FCSTD DOCUMENT  (FreeCAD 1.1R40971 (Git))
Label: pole-barn-interior2
License: All rights reserved
LicenseURL: https://en.wikipedia.org/wiki/All_rights_reserved
objects: App::Point×1, Sketcher::SketchObject×1, PartDesign::Body×1
note: 3 computed .brp shape members not serialized (recipe doc carries the construction recipe); baked Part::Feature solids carry a one-line shape summary decoded from their .brp

FEATURE [App::Point] Origin001
  Role = Origin
FEATURE [Sketcher::SketchObject] Sketch
  ArcFitTolerance = 1e-06
  AttachmentSupport = -> [XY_Plane]
  ExternalTypes = [0]
  FullyConstrained = false
  MakeInternals = false
  MapMode = 5
  sketch-geometry (89):
    g0: LineSegment StartX=4876.8 StartY=439.251 StartZ=0 EndX=4991.1 EndY=439.251 EndZ=0
    g1: LineSegment StartX=4991.1 StartY=439.251 StartZ=0 EndX=4991.1 EndY=629.751 EndZ=0
    g2: LineSegment StartX=4991.1 StartY=629.751 StartZ=0 EndX=4876.8 EndY=629.751 EndZ=0
    g3: LineSegment StartX=4876.8 StartY=629.751 StartZ=0 EndX=4876.8 EndY=439.251 EndZ=0
    g4: LineSegment StartX=-4876.8 StartY=-8343.9 StartZ=0 EndX=4876.8 EndY=-8343.9 EndZ=0
    g5: LineSegment StartX=4876.8 StartY=-8343.9 StartZ=0 EndX=4876.8 EndY=8343.9 EndZ=0
    g6: LineSegment StartX=4876.8 StartY=8343.9 StartZ=0 EndX=-4876.8 EndY=8343.9 EndZ=0
    g7: LineSegment StartX=-4876.8 StartY=8343.9 StartZ=0 EndX=-4876.8 EndY=-8343.9 EndZ=0
    g8: GeomPoint [constr] X=0 Y=0 Z=0
    g9: LineSegment StartX=-5817.55 StartY=9316.89 StartZ=0 EndX=-5703.25 EndY=9316.89 EndZ=0
    g10: LineSegment StartX=-5703.25 StartY=9316.89 StartZ=0 EndX=-5703.25 EndY=9507.39 EndZ=0
    g11: LineSegment StartX=-5703.25 StartY=9507.39 StartZ=0 EndX=-5817.55 EndY=9507.39 EndZ=0
    g12: LineSegment StartX=-5817.55 StartY=9507.39 StartZ=0 EndX=-5817.55 EndY=9316.89 EndZ=0
    g13: LineSegment StartX=-6563.87 StartY=-9198.88 StartZ=0 EndX=-6449.57 EndY=-9198.88 EndZ=0
    g14: LineSegment StartX=-6449.57 StartY=-9198.88 StartZ=0 EndX=-6449.57 EndY=-9008.38 EndZ=0
    g15: LineSegment StartX=-6449.57 StartY=-9008.38 StartZ=0 EndX=-6563.87 EndY=-9008.38 EndZ=0
    g16: LineSegment StartX=-6563.87 StartY=-9008.38 StartZ=0 EndX=-6563.87 EndY=-9198.88 EndZ=0
    g17: LineSegment StartX=6443.37 StartY=-8807.95 StartZ=0 EndX=6557.67 EndY=-8807.95 EndZ=0
    g18: LineSegment StartX=6557.67 StartY=-8807.95 StartZ=0 EndX=6557.67 EndY=-8617.45 EndZ=0
    g19: LineSegment StartX=6557.67 StartY=-8617.45 StartZ=0 EndX=6443.37 EndY=-8617.45 EndZ=0
    g20: LineSegment StartX=6443.37 StartY=-8617.45 StartZ=0 EndX=6443.37 EndY=-8807.95 EndZ=0
    g21: LineSegment StartX=3028.84 StartY=8343.9 StartZ=0 EndX=3143.14 EndY=8343.9 EndZ=0
    g22: LineSegment StartX=3143.14 StartY=8343.9 StartZ=0 EndX=3143.14 EndY=8534.4 EndZ=0
    g23: LineSegment StartX=3143.14 StartY=8534.4 StartZ=0 EndX=3028.84 EndY=8534.4 EndZ=0
    g24: LineSegment StartX=3028.84 StartY=8534.4 StartZ=0 EndX=3028.84 EndY=8343.9 EndZ=0
    g25: LineSegment StartX=1020.89 StartY=8343.9 StartZ=0 EndX=1135.19 EndY=8343.9 EndZ=0
    g26: LineSegment StartX=1135.19 StartY=8343.9 StartZ=0 EndX=1135.19 EndY=8534.4 EndZ=0
    g27: LineSegment StartX=1135.19 StartY=8534.4 StartZ=0 EndX=1020.89 EndY=8534.4 EndZ=0
    g28: LineSegment StartX=1020.89 StartY=8534.4 StartZ=0 EndX=1020.89 EndY=8343.9 EndZ=0
    g29: LineSegment StartX=-1289.14 StartY=8343.9 StartZ=0 EndX=-1174.84 EndY=8343.9 EndZ=0
    g30: LineSegment StartX=-1174.84 StartY=8343.9 StartZ=0 EndX=-1174.84 EndY=8534.4 EndZ=0
    g31: LineSegment StartX=-1174.84 StartY=8534.4 StartZ=0 EndX=-1289.14 EndY=8534.4 EndZ=0
    g32: LineSegment StartX=-1289.14 StartY=8534.4 StartZ=0 EndX=-1289.14 EndY=8343.9 EndZ=0
    g33: LineSegment StartX=-3969.53 StartY=8343.9 StartZ=0 EndX=-3855.23 EndY=8343.9 EndZ=0
    g34: LineSegment StartX=-3855.23 StartY=8343.9 StartZ=0 EndX=-3855.23 EndY=8534.4 EndZ=0
    g35: LineSegment StartX=-3855.23 StartY=8534.4 StartZ=0 EndX=-3969.53 EndY=8534.4 EndZ=0
    g36: LineSegment StartX=-3969.53 StartY=8534.4 StartZ=0 EndX=-3969.53 EndY=8343.9 EndZ=0
    g37: LineSegment StartX=4876.8 StartY=-2521.71 StartZ=0 EndX=4991.1 EndY=-2521.71 EndZ=0
    g38: LineSegment StartX=4991.1 StartY=-2521.71 StartZ=0 EndX=4991.1 EndY=-2331.21 EndZ=0
    g39: LineSegment StartX=4991.1 StartY=-2331.21 StartZ=0 EndX=4876.8 EndY=-2331.21 EndZ=0
    g40: LineSegment StartX=4876.8 StartY=-2331.21 StartZ=0 EndX=4876.8 EndY=-2521.71 EndZ=0
    g41: LineSegment StartX=4876.8 StartY=-6117.69 StartZ=0 EndX=4991.1 EndY=-6117.69 EndZ=0
    g42: LineSegment StartX=4991.1 StartY=-6117.69 StartZ=0 EndX=4991.1 EndY=-5927.19 EndZ=0
    g43: LineSegment StartX=4991.1 StartY=-5927.19 StartZ=0 EndX=4876.8 EndY=-5927.19 EndZ=0
    g44: LineSegment StartX=4876.8 StartY=-5927.19 StartZ=0 EndX=4876.8 EndY=-6117.69 EndZ=0
    g45: LineSegment StartX=3028.84 StartY=-8534.4 StartZ=0 EndX=3143.14 EndY=-8534.4 EndZ=0
    g46: LineSegment StartX=3143.14 StartY=-8534.4 StartZ=0 EndX=3143.14 EndY=-8343.9 EndZ=0
    g47: LineSegment StartX=3143.14 StartY=-8343.9 StartZ=0 EndX=3028.84 EndY=-8343.9 EndZ=0
    g48: LineSegment StartX=3028.84 StartY=-8343.9 StartZ=0 EndX=3028.84 EndY=-8534.4 EndZ=0
    g49: LineSegment StartX=1020.89 StartY=-8534.4 StartZ=0 EndX=1135.19 EndY=-8534.4 EndZ=0
    g50: LineSegment StartX=1135.19 StartY=-8534.4 StartZ=0 EndX=1135.19 EndY=-8343.9 EndZ=0
    g51: LineSegment StartX=1135.19 StartY=-8343.9 StartZ=0 EndX=1020.89 EndY=-8343.9 EndZ=0
    g52: LineSegment StartX=1020.89 StartY=-8343.9 StartZ=0 EndX=1020.89 EndY=-8534.4 EndZ=0
    g53: LineSegment StartX=-2728.47 StartY=-8534.4 StartZ=0 EndX=-2614.17 EndY=-8534.4 EndZ=0
    g54: LineSegment StartX=-2614.17 StartY=-8534.4 StartZ=0 EndX=-2614.17 EndY=-8343.9 EndZ=0
    g55: LineSegment StartX=-2614.17 StartY=-8343.9 StartZ=0 EndX=-2728.47 EndY=-8343.9 EndZ=0
    g56: LineSegment StartX=-2728.47 StartY=-8343.9 StartZ=0 EndX=-2728.47 EndY=-8534.4 EndZ=0
    g57: LineSegment StartX=-4991.1 StartY=-6117.69 StartZ=0 EndX=-4876.8 EndY=-6117.69 EndZ=0
    g58: LineSegment StartX=-4876.8 StartY=-6117.69 StartZ=0 EndX=-4876.8 EndY=-5927.19 EndZ=0
    g59: LineSegment StartX=-4876.8 StartY=-5927.19 StartZ=0 EndX=-4991.1 EndY=-5927.19 EndZ=0
    g60: LineSegment StartX=-4991.1 StartY=-5927.19 StartZ=0 EndX=-4991.1 EndY=-6117.69 EndZ=0
    g61: LineSegment StartX=-4991.1 StartY=-2521.71 StartZ=0 EndX=-4876.8 EndY=-2521.71 EndZ=0
    g62: LineSegment StartX=-4876.8 StartY=-2521.71 StartZ=0 EndX=-4876.8 EndY=-2331.21 EndZ=0
    g63: LineSegment StartX=-4876.8 StartY=-2331.21 StartZ=0 EndX=-4991.1 EndY=-2331.21 EndZ=0
    g64: LineSegment StartX=-4991.1 StartY=-2331.21 StartZ=0 EndX=-4991.1 EndY=-2521.71 EndZ=0
    g65: LineSegment StartX=-4991.1 StartY=3541.08 StartZ=0 EndX=-4876.8 EndY=3541.08 EndZ=0
    g66: LineSegment StartX=-4876.8 StartY=3541.08 StartZ=0 EndX=-4876.8 EndY=3731.58 EndZ=0
    g67: LineSegment StartX=-4876.8 StartY=3731.58 StartZ=0 EndX=-4991.1 EndY=3731.58 EndZ=0
    g68: LineSegment StartX=-4991.1 StartY=3731.58 StartZ=0 EndX=-4991.1 EndY=3541.08 EndZ=0
    g69: LineSegment StartX=-4991.1 StartY=5815.59 StartZ=0 EndX=-4876.8 EndY=5815.59 EndZ=0
    g70: LineSegment StartX=-4876.8 StartY=5815.59 StartZ=0 EndX=-4876.8 EndY=6006.09 EndZ=0
    g71: LineSegment StartX=-4876.8 StartY=6006.09 StartZ=0 EndX=-4991.1 EndY=6006.09 EndZ=0
    g72: LineSegment StartX=-4991.1 StartY=6006.09 StartZ=0 EndX=-4991.1 EndY=5815.59 EndZ=0
    g73: LineSegment StartX=4876.8 StartY=3541.08 StartZ=0 EndX=4991.1 EndY=3541.08 EndZ=0
    g74: LineSegment StartX=4991.1 StartY=3541.08 StartZ=0 EndX=4991.1 EndY=3731.58 EndZ=0
    g75: LineSegment StartX=4991.1 StartY=3731.58 StartZ=0 EndX=4876.8 EndY=3731.58 EndZ=0
    g76: LineSegment StartX=4876.8 StartY=3731.58 StartZ=0 EndX=4876.8 EndY=3541.08 EndZ=0
    g77: LineSegment StartX=4876.8 StartY=5815.59 StartZ=0 EndX=4991.1 EndY=5815.59 EndZ=0
    g78: LineSegment StartX=4991.1 StartY=5815.59 StartZ=0 EndX=4991.1 EndY=6006.09 EndZ=0
    g79: LineSegment StartX=4991.1 StartY=6006.09 StartZ=0 EndX=4876.8 EndY=6006.09 EndZ=0
    g80: LineSegment StartX=4876.8 StartY=6006.09 StartZ=0 EndX=4876.8 EndY=5815.59 EndZ=0
    g81: LineSegment StartX=-4991.1 StartY=439.251 StartZ=0 EndX=-4876.8 EndY=439.251 EndZ=0
    g82: LineSegment StartX=-4876.8 StartY=439.251 StartZ=0 EndX=-4876.8 EndY=629.751 EndZ=0
    g83: LineSegment StartX=-4876.8 StartY=629.751 StartZ=0 EndX=-4991.1 EndY=629.751 EndZ=0
    g84: LineSegment StartX=-4991.1 StartY=629.751 StartZ=0 EndX=-4991.1 EndY=439.251 EndZ=0
    g85: LineSegment StartX=5981.37 StartY=9050.35 StartZ=0 EndX=6095.67 EndY=9050.35 EndZ=0
    g86: LineSegment StartX=6095.67 StartY=9050.35 StartZ=0 EndX=6095.67 EndY=9240.85 EndZ=0
    g87: LineSegment StartX=6095.67 StartY=9240.85 StartZ=0 EndX=5981.37 EndY=9240.85 EndZ=0
    g88: LineSegment StartX=5981.37 StartY=9240.85 StartZ=0 EndX=5981.37 EndY=9050.35 EndZ=0
  constraints (246):
    c: Coincident(g0,g1)
    c: Coincident(g1,g2)
    c: Coincident(g2,g3)
    c: Coincident(g3,g0)
    c: Horizontal(g0)
    c: Horizontal(g2)
    c: Vertical(g1)
    c: Vertical(g3)
    c: Distance(g1,g3) = 114.3
    c: Distance(g0,g2) = 190.5
    c: Coincident(g4,g5)
    c: Coincident(g5,g6)
    c: Coincident(g6,g7)
    c: Coincident(g7,g4)
    c: Horizontal(g4)
    c: Horizontal(g6)
    c: Vertical(g5)
    c: Vertical(g7)
    c: Symmetric(g6,g4,g8)
    c: Distance(g5,g7) = 9753.6
    c: Distance(g4,g6) = 16687.8
    c: Coincident(g8,g-1)
    c: Coincident(g9,g10)
    c: Coincident(g10,g11)
    c: Coincident(g11,g12)
    c: Coincident(g12,g9)
    c: Horizontal(g9)
    c: Horizontal(g11)
    c: Vertical(g10)
    c: Vertical(g12)
    c: Distance(g10,g12) = 114.3
    c: Distance(g9,g11) = 190.5
    c: Coincident(g13,g14)
    c: Coincident(g14,g15)
    c: Coincident(g15,g16)
    c: Coincident(g16,g13)
    c: Horizontal(g13)
    c: Horizontal(g15)
    c: Vertical(g14)
    c: Vertical(g16)
    c: Distance(g14,g16) = 114.3
    c: Distance(g13,g15) = 190.5
    c: Coincident(g17,g18)
    c: Coincident(g18,g19)
    c: Coincident(g19,g20)
    c: Coincident(g20,g17)
    c: Horizontal(g17)
    c: Horizontal(g19)
    c: Vertical(g18)
    c: Vertical(g20)
    c: Distance(g18,g20) = 114.3
    c: Distance(g17,g19) = 190.5
    c: Coincident(g21,g22)
    c: Coincident(g22,g23)
    c: Coincident(g23,g24)
    c: Coincident(g24,g21)
    c: Horizontal(g21)
    c: Horizontal(g23)
    c: Vertical(g22)
    c: Vertical(g24)
    c: Distance(g22,g24) = 114.3
    c: Distance(g21,g23) = 190.5
    c: Coincident(g25,g26)
    c: Coincident(g26,g27)
    c: Coincident(g27,g28)
    c: Coincident(g28,g25)
    c: Horizontal(g25)
    c: Horizontal(g27)
    c: Vertical(g26)
    c: Vertical(g28)
    c: Distance(g26,g28) = 114.3
    c: Distance(g25,g27) = 190.5
    c: Coincident(g29,g30)
    c: Coincident(g30,g31)
    c: Coincident(g31,g32)
    c: Coincident(g32,g29)
    c: Horizontal(g29)
    c: Horizontal(g31)
    c: Vertical(g30)
    c: Vertical(g32)
    c: Distance(g30,g32) = 114.3
    c: Distance(g29,g31) = 190.5
    c: Coincident(g33,g34)
    c: Coincident(g34,g35)
    c: Coincident(g35,g36)
    c: Coincident(g36,g33)
    c: Horizontal(g33)
    c: Horizontal(g35)
    c: Vertical(g34)
    c: Vertical(g36)
    c: Distance(g34,g36) = 114.3
    c: Distance(g33,g35) = 190.5
    c: Coincident(g37,g38)
    c: Coincident(g38,g39)
    c: Coincident(g39,g40)
    c: Coincident(g40,g37)
    c: Horizontal(g37)
    c: Horizontal(g39)
    c: Vertical(g38)
    c: Vertical(g40)
    c: Distance(g38,g40) = 114.3
    c: Distance(g37,g39) = 190.5
    c: Coincident(g41,g42)
    c: Coincident(g42,g43)
    c: Coincident(g43,g44)
    c: Coincident(g44,g41)
    c: Horizontal(g41)
    c: Horizontal(g43)
    c: Vertical(g42)
    c: Vertical(g44)
    c: Distance(g42,g44) = 114.3
    c: Distance(g41,g43) = 190.5
    c: Coincident(g45,g46)
    c: Coincident(g46,g47)
    c: Coincident(g47,g48)
    c: Coincident(g48,g45)
    c: Horizontal(g45)
    c: Horizontal(g47)
    c: Vertical(g46)
    c: Vertical(g48)
    c: Distance(g46,g48) = 114.3
    c: Distance(g45,g47) = 190.5
    c: Coincident(g49,g50)
    c: Coincident(g50,g51)
    c: Coincident(g51,g52)
    c: Coincident(g52,g49)
    c: Horizontal(g49)
    c: Horizontal(g51)
    c: Vertical(g50)
    c: Vertical(g52)
    c: Distance(g50,g52) = 114.3
    c: Distance(g49,g51) = 190.5
    c: Coincident(g53,g54)
    c: Coincident(g54,g55)
    c: Coincident(g55,g56)
    c: Coincident(g56,g53)
    c: Horizontal(g53)
    c: Horizontal(g55)
    c: Vertical(g54)
    c: Vertical(g56)
    c: Distance(g54,g56) = 114.3
    c: Distance(g53,g55) = 190.5
    c: Coincident(g57,g58)
    c: Coincident(g58,g59)
    c: Coincident(g59,g60)
    c: Coincident(g60,g57)
    c: Horizontal(g57)
    c: Horizontal(g59)
    c: Vertical(g58)
    c: Vertical(g60)
    c: Distance(g58,g60) = 114.3
    c: Distance(g57,g59) = 190.5
    c: Coincident(g61,g62)
    c: Coincident(g62,g63)
    c: Coincident(g63,g64)
    c: Coincident(g64,g61)
    c: Horizontal(g61)
    c: Horizontal(g63)
    c: Vertical(g62)
    c: Vertical(g64)
    c: Distance(g62,g64) = 114.3
    c: Distance(g61,g63) = 190.5
    c: Coincident(g65,g66)
    c: Coincident(g66,g67)
    c: Coincident(g67,g68)
    c: Coincident(g68,g65)
    c: Horizontal(g65)
    c: Horizontal(g67)
    c: Vertical(g66)
    c: Vertical(g68)
    c: Distance(g66,g68) = 114.3
    c: Distance(g65,g67) = 190.5
    c: Coincident(g69,g70)
    c: Coincident(g70,g71)
    c: Coincident(g71,g72)
    c: Coincident(g72,g69)
    c: Horizontal(g69)
    c: Horizontal(g71)
    c: Vertical(g70)
    c: Vertical(g72)
    c: Distance(g70,g72) = 114.3
    c: Distance(g69,g71) = 190.5
    c: Vertical(g21,g46)
    c: Vertical(g50,g25)
    c: Horizontal(g58,g43)
    c: PointOnObject(g33,g6)
    c: PointOnObject(g29,g6)
    c: PointOnObject(g25,g6)
    c: PointOnObject(g21,g6)
    c: Coincident(g73,g74)
    c: Coincident(g74,g75)
    c: Coincident(g75,g76)
    c: Coincident(g76,g73)
    c: Horizontal(g73)
    c: Horizontal(g75)
    c: Vertical(g74)
    c: Vertical(g76)
    c: Distance(g74,g76) = 114.3
    c: Distance(g73,g75) = 190.5
    c: Coincident(g77,g78)
    c: Coincident(g78,g79)
    c: Coincident(g79,g80)
    c: Coincident(g80,g77)
    c: Horizontal(g77)
    c: Horizontal(g79)
    c: Vertical(g78)
    c: Vertical(g80)
    c: Distance(g78,g80) = 114.3
    c: Distance(g77,g79) = 190.5
    c: Coincident(g81,g82)
    c: Coincident(g82,g83)
    c: Coincident(g83,g84)
    c: Coincident(g84,g81)
    c: Horizontal(g81)
    c: Horizontal(g83)
    c: Vertical(g82)
    c: Vertical(g84)
    c: Distance(g82,g84) = 114.3
    c: Distance(g81,g83) = 190.5
    c: Coincident(g85,g86)
    c: Coincident(g86,g87)
    c: Coincident(g87,g88)
    c: Coincident(g88,g85)
    c: Horizontal(g85)
    c: Horizontal(g87)
    c: Vertical(g86)
    c: Vertical(g88)
    c: Distance(g86,g88) = 114.3
    c: Distance(g85,g87) = 190.5
    c: Horizontal(g82,g2)
    c: Horizontal(g70,g79)
    c: Horizontal(g66,g75)
    c: Horizontal(g62,g39)
    c: PointOnObject(g70,g7)
    c: PointOnObject(g66,g7)
    c: PointOnObject(g82,g7)
    c: PointOnObject(g62,g7)
    c: PointOnObject(g58,g7)
    c: PointOnObject(g54,g4)
    c: PointOnObject(g50,g4)
    c: PointOnObject(g46,g4)
    c: PointOnObject(g43,g5)
    c: PointOnObject(g39,g5)
    c: PointOnObject(g2,g5)
    c: PointOnObject(g75,g5)
    c: PointOnObject(g79,g5)
FEATURE [PartDesign::Body] Body
  AllowCompound = false
  Group = -> [Sketch]
  Origin = -> Origin
